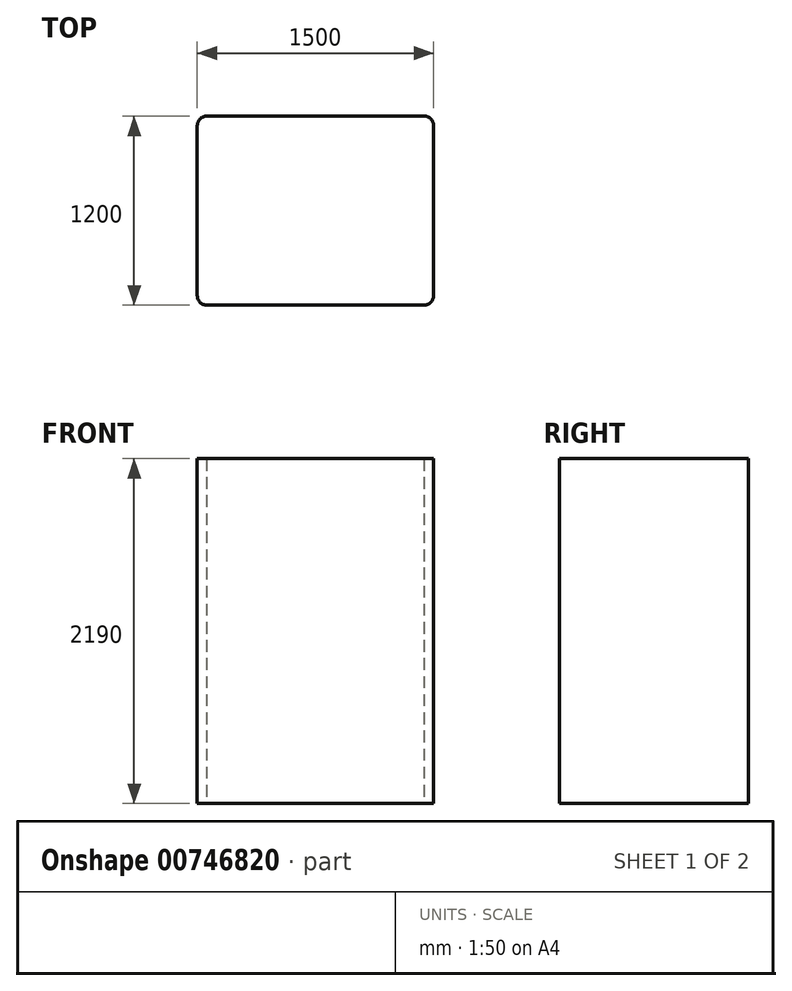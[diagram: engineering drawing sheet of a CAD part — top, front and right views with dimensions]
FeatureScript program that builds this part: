
annotation { "Feature Type Name" : "Feature", "Feature Type Description" : "" }
export const myFeature = defineFeature(function(context is Context, id is Id, definition is map)
    precondition{}
    {
        {
            var Q0;
            Q0=qCreatedBy(makeId("Top.planeOp"),FACE);
            var sketch = newSketch(context, id + "F0", { "sketchPlane" : qUnion([Q0])});
            skLineSegment(sketch, "E0.bottom", {"start": v(-690, 600) * mm, "end": v(690, 600) * mm});
            skLineSegment(sketch, "E0.top", {"start": v(-690, -600) * mm, "end": v(690, -600) * mm});
            skLineSegment(sketch, "E0.left", {"start": v(-750, 540) * mm, "end": v(-750, -540) * mm});
            skLineSegment(sketch, "E0.right", {"start": v(750, 540) * mm, "end": v(750, -540) * mm});
            skLineSegment(sketch, "E1", {"start": v(0, 1841.7) * mm, "end": v(0, -1656.37) * mm, "construction": true});
            skLineSegment(sketch, "E2", {"start": v(-1586.87, 0) * mm, "end": v(1741.31, 0) * mm, "construction": true});
            skPoint(sketch, "E3.visualSharp", {"position": v(-750, 600) * mm});
            skArc(sketch, "E3.filletArc", {"start": v(-690, 600) * mm, "mid": v(-732.43, 582.43) * mm, "end": v(-750, 540) * mm});
            skPoint(sketch, "E4.visualSharp", {"position": v(750, 600) * mm});
            skArc(sketch, "E4.filletArc", {"start": v(750, 540) * mm, "mid": v(732.43, 582.43) * mm, "end": v(690, 600) * mm});
            skPoint(sketch, "E5.visualSharp", {"position": v(750, -600) * mm});
            skArc(sketch, "E5.filletArc", {"start": v(690, -600) * mm, "mid": v(732.43, -582.43) * mm, "end": v(750, -540) * mm});
            skPoint(sketch, "E6.visualSharp", {"position": v(-750, -600) * mm});
            skArc(sketch, "E6.filletArc", {"start": v(-750, -540) * mm, "mid": v(-732.43, -582.43) * mm, "end": v(-690, -600) * mm});
            skSolve(sketch);
        }
        {
            var Q0;
            Q0 = qSketchRegion(id + "F0", true);
            extrude(context, id + "F1", {"entities" : qUnion([Q0]), "depth" : 2190 * mm, "offsetDistance" : 25.4 * mm});
        }
        {
            var Q0;
            Q0=makeQuery(id+"F1.opExtrude","SWEPT_FACE",FACE,{"disambiguationData":[OSD([sQuery(id+"F0.wireOp",EDGE,"E0.bottom")])]});
            shell(context, id + "F2", {"entities" : qUnion([Q0]), "thickness" : 2.54 * mm});
        }
    });
